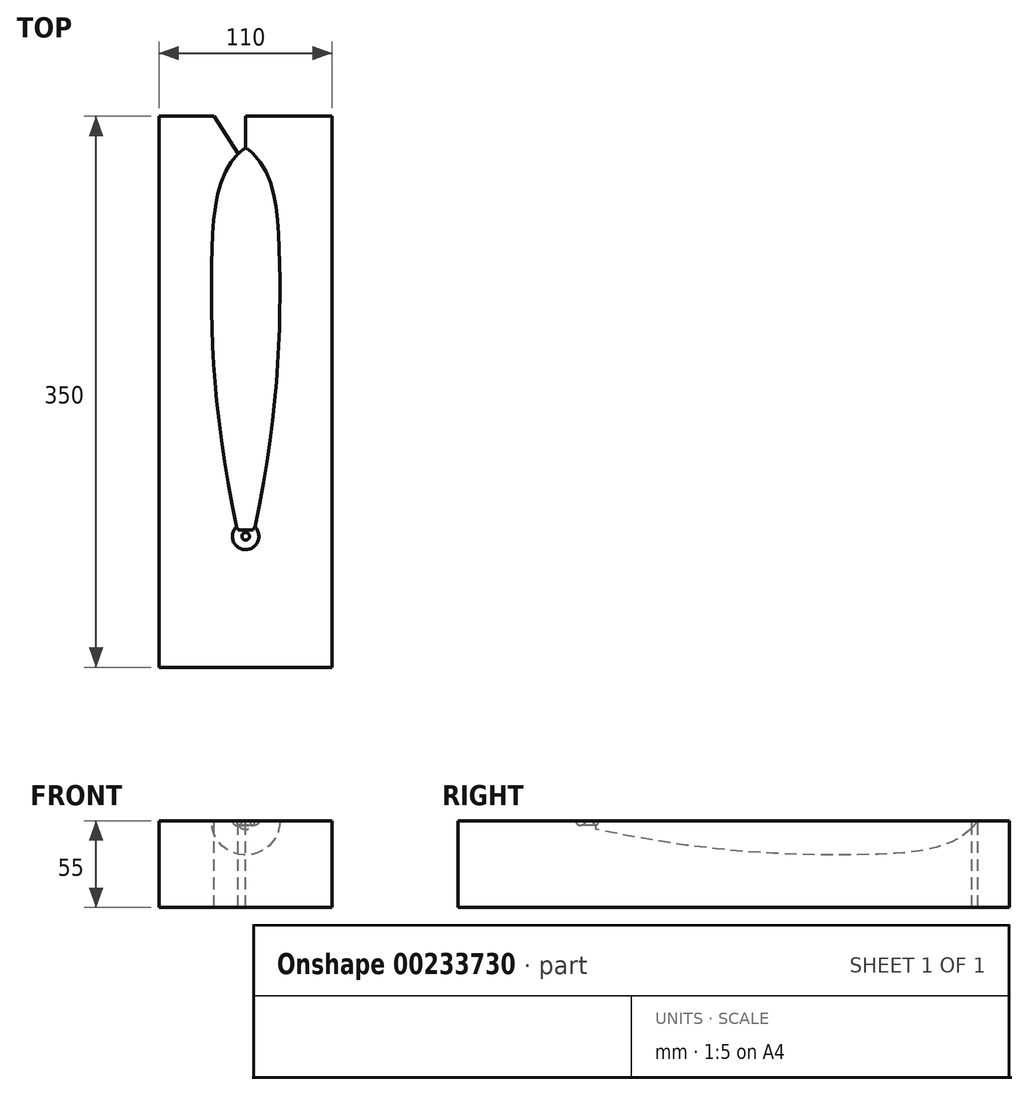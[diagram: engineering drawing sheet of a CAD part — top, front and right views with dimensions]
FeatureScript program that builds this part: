
annotation { "Feature Type Name" : "Feature", "Feature Type Description" : "" }
export const myFeature = defineFeature(function(context is Context, id is Id, definition is map)
    precondition{}
    {
        {
            var Q0;
            Q0=qCreatedBy(makeId("Top.planeOp"),FACE);
            var sketch = newSketch(context, id + "F0", { "sketchPlane" : qUnion([Q0])});
            skLineSegment(sketch, "E0", {"start": v(0, 246.88) * mm, "end": v(0, 4.18) * mm});
            skPoint(sketch, "E1", {"position": v(0, 176.88) * mm});
            skPoint(sketch, "E2", {"position": v(0, 1.88) * mm});
            skPoint(sketch, "E3", {"position": v(-21.5, 176.88) * mm});
            skFitSpline(sketch, "E4", {"points": [v(0, 246.88) * mm, v(-21.5, 176.88) * mm, v(-5, 1.88) * mm], "startDerivative": vector(-143.64, -99.23) * mm, "endDerivative": vector(77.1, -353.38) * mm});
            skPoint(sketch, "E5.bottom.start.orphan", {"position": v(123.59, 246.88) * mm});
            skLineSegment(sketch, "E6", {"start": v(0, 246.88) * mm, "end": v(0, 266.88) * mm});
            skLineSegment(sketch, "E7", {"start": v(0, 266.88) * mm, "end": v(-55, 266.88) * mm});
            skLineSegment(sketch, "E8", {"start": v(-55, 266.88) * mm, "end": v(-55, -83.12) * mm});
            skLineSegment(sketch, "E9", {"start": v(-55, -83.12) * mm, "end": v(55, -83.12) * mm});
            skLineSegment(sketch, "E10", {"start": v(55, -83.12) * mm, "end": v(55, 266.88) * mm});
            skLineSegment(sketch, "E11", {"start": v(55, 266.88) * mm, "end": v(0, 266.88) * mm});
            skLineSegment(sketch, "E12", {"start": v(-4.75, 242.98) * mm, "end": v(-20, 266.88) * mm});
            skPoint(sketch, "E13.trimOffspring.end.orphan", {"position": v(0, -3.12) * mm});
            skLineSegment(sketch, "E14", {"start": v(0, 4.18) * mm, "end": v(-5.5, 4.18) * mm});
            skSolve(sketch);
        }
        {
            var Q0;
            Q0=makeQuery(id+"F0.imprint","IMPRINT",FACE,{"disambiguationData":[TD([[makeQuery(id+"F0.imprint","IMPRINT",EDGE,{"derivedFrom":sQuery(id+"F0.wireOp",EDGE,"E0")}),1.0]])]});
            var Q1;
            Q1=makeQuery(id+"F0.imprint","IMPRINT",FACE,{"disambiguationData":[TD([[makeQuery(id+"F0.imprint","IMPRINT",EDGE,{"derivedFrom":sQuery(id+"F0.wireOp",EDGE,"E0")}),-1.0]])]});
            extrude(context, id + "F1", {"entities" : qUnion([Q0, Q1]), "depth" : 55 * mm});
        }
        {
            var Q0;
            Q0=makeQuery(id+"F0.imprint","IMPRINT",FACE,{"disambiguationData":[TD([[makeQuery(id+"F0.imprint","IMPRINT",EDGE,{"derivedFrom":sQuery(id+"F0.wireOp",EDGE,"E0")}),-1.0]])]});
            var Q1;
            Q1=sQuery(id+"F0.wireOp",EDGE,"E0");
            revolve(context, id + "F2", {"operationType" : NewBodyOperationType.REMOVE, "entities" : qUnion([Q0]), "axis" : qUnion([Q1]), "revolveType" : RevolveType.FULL, "oppositeDirection" : true});
        }
        {
            var Q0;
            Q0=qCreatedBy(makeId("Top.planeOp"),FACE);
            var sketch = newSketch(context, id + "F3", { "sketchPlane" : qUnion([Q0])});
            skLineSegment(sketch, "E15", {"start": v(-23.37, 0) * mm, "end": v(36.52, 0) * mm});
            skPoint(sketch, "E16", {"position": v(-4.16, 0) * mm});
            skSolve(sketch);
        }
        {
            var Q0;
            Q0=sQuery(id+"F3.wireOp",EDGE,"E15");
            cPlane(context, id + "F4", {"entities" : qUnion([Q0]), "cplaneType" : CPlaneType.LINE_ANGLE, "offset" : 25 * mm, "angle" : 180 * degree, "width" : 150 * mm, "height" : 150 * mm});
        }
        {
            var Q0;
            Q0=qCreatedBy(id+"F4.planeOp",FACE);
            var sketch = newSketch(context, id + "F5", { "sketchPlane" : qUnion([Q0])});
            skCircle(sketch, "E17", {"center": v(-5.42, 0) * mm, "radius": 3 * mm});
            skPoint(sketch, "E18", {"position": v(-1.27, 0) * mm});
            skSolve(sketch);
        }
        {
            var Q0;
            Q0=qCreatedBy(makeId("Top.planeOp"),FACE);
            var sketch = newSketch(context, id + "F6", { "sketchPlane" : qUnion([Q0])});
            skCircle(sketch, "E19", {"center": v(0, 0) * mm, "radius": 4.02 * mm});
            skSolve(sketch);
        }
        {
            var Q0;
            Q0=makeQuery(id+"F5.imprint","IMPRINT",FACE,{"disambiguationData":[TD([[makeQuery(id+"F5.imprint","IMPRINT",EDGE,{"derivedFrom":sQuery(id+"F5.wireOp",EDGE,"E17")}),1.0]])]});
            var Q1;
            Q1=sQuery(id+"F6.wireOp",EDGE,"E19");
            sweep(context, id + "F7", {"operationType" : NewBodyOperationType.REMOVE, "profiles" : qUnion([Q0]), "path" : qUnion([Q1])});
        }
        {
            var Q0;
            Q0=makeQuery(id+"F1.opExtrude","SWEPT_BODY",BODY,{"disambiguationData":[OSD([sQuery(id+"F0.wireOp",EDGE,"E7"),sQuery(id+"F0.wireOp",EDGE,"E8"),sQuery(id+"F0.wireOp",EDGE,"E9"),sQuery(id+"F0.wireOp",EDGE,"E10"),sQuery(id+"F0.wireOp",EDGE,"E11")])]});
            var Q1;
            Q1=makeQuery(id+"F0.imprint","IMPRINT",FACE,{"disambiguationData":[TD([[makeQuery(id+"F0.imprint","IMPRINT",EDGE,{"derivedFrom":sQuery(id+"F0.wireOp",EDGE,"E0")}),1.0]])]});
            mirror(context, id + "F8", {"entities" : qUnion([Q0]), "mirrorPlane" : qUnion([Q1])});
        }
        {
            var Q0;
            Q0=makeQuery(id+"F1.opExtrude","SWEPT_BODY",BODY,{"disambiguationData":[OSD([sQuery(id+"F0.wireOp",EDGE,"E7"),sQuery(id+"F0.wireOp",EDGE,"E8"),sQuery(id+"F0.wireOp",EDGE,"E9"),sQuery(id+"F0.wireOp",EDGE,"E10"),sQuery(id+"F0.wireOp",EDGE,"E11")])]});
            deleteBodies(context, id + "F9", {"entities" : qUnion([Q0])});
        }
    });
